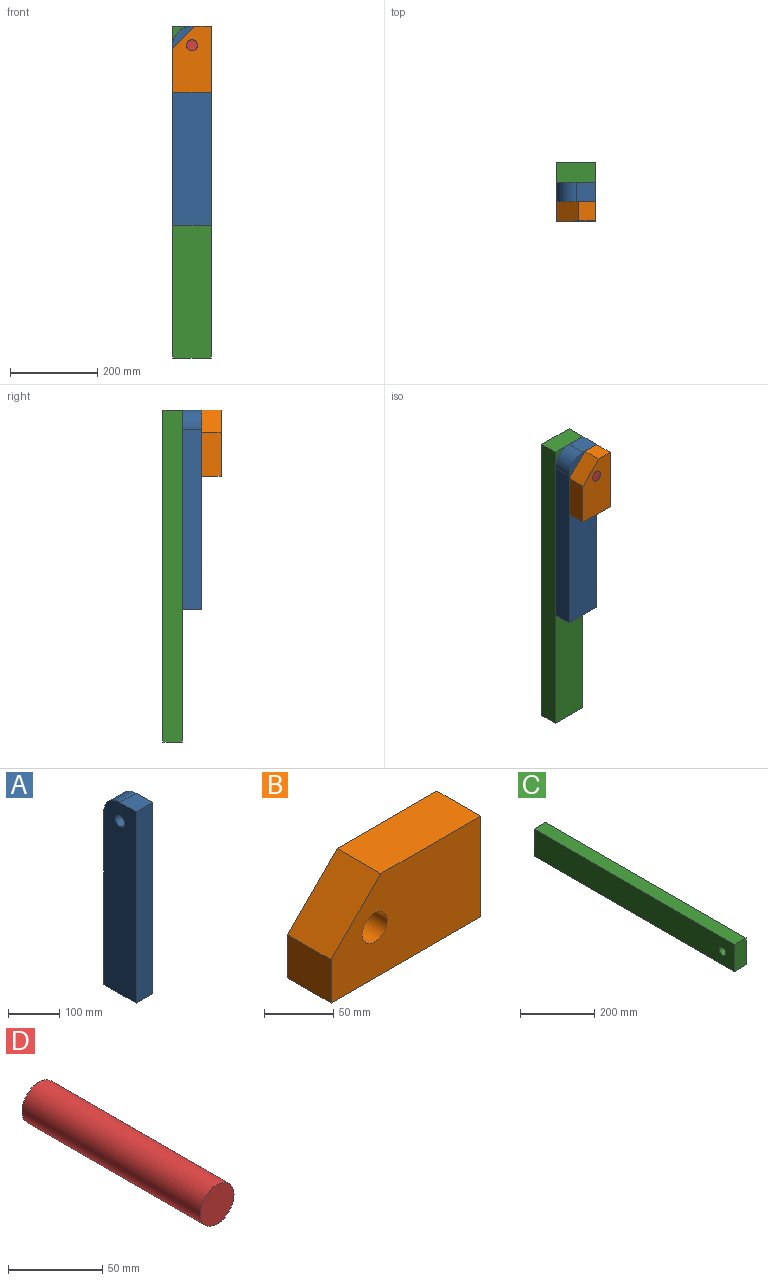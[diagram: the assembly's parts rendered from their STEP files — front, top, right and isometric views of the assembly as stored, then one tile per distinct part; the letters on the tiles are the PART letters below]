
ASSEMBLY  parts=4 mates=3
PART A: 8 faces, bbox 44.5x88.9x457.2 mm
  f0: plane 44.45x44.45mm, normal (0,0,1), area 1975.8mm2, adj f1,f5,f6,f7
  f1: plane 457.2x44.45mm, normal (0,-1,0), area 20322.5mm2, adj f0,f2,f6,f7
  f2: plane 88.9x44.45mm, normal (0,0,-1), area 3951.6mm2, adj f1,f3,f6,f7
  f3: plane 412.75x44.45mm, normal (0,1,0), area 18346.7mm2, adj f2,f5,f6,f7
  f4: cylinder r=12.7mm len=44.45mm, axis (-1,0,0), area 3547mm2, adj f6,f7
  f5: cylinder r=44.45mm len=44.45mm, axis (-1,0,0), area 3103.6mm2, adj f0,f3,f6,f7
  f6: plane 457.2x88.9mm, normal (1,0,0), area 39714.4mm2, adj f0,f1,f2,f3,f4,f5
  f7: plane 457.2x88.9mm, normal (-1,0,0), area 39714.4mm2, adj f0,f1,f2,f3,f4,f5
PART B: 8 faces, bbox 152.4x44.5x88.9 mm
  f0: plane 101.6x44.45mm, normal (0,0,1), area 4516.1mm2, adj f1,f4,f6,f7
  f1: plane 50.8x50.8mm, normal (-0.71,0,0.71), area 3193.4mm2, adj f0,f2,f6,f7
  f2: plane 44.45x38.1mm, normal (-1,0,0), area 1693.5mm2, adj f1,f3,f6,f7
  f3: plane 152.4x44.45mm, normal (0,0,-1), area 6774.2mm2, adj f2,f4,f6,f7
  f4: plane 88.9x44.45mm, normal (1,0,0), area 3951.6mm2, adj f0,f3,f6,f7
  f5: cylinder r=12.7mm len=44.45mm, axis (0,1,0), area 3547mm2, adj f6,f7
  f6: plane 152.4x88.9mm, normal (0,-1,0), area 11751.3mm2, adj f0,f1,f2,f3,f4,f5
  f7: plane 152.4x88.9mm, normal (0,1,0), area 11751.3mm2, adj f0,f1,f2,f3,f4,f5
PART C: 7 faces, bbox 44.5x762x88.9 mm
  f0: plane 762x88.9mm, normal (-1,0,0), area 67235.1mm2, adj f1,f3,f4,f5,f6
  f1: plane 762x44.45mm, normal (0,0,-1), area 33870.9mm2, adj f0,f2,f4,f5
  f2: plane 762x88.9mm, normal (1,0,0), area 67235.1mm2, adj f1,f3,f4,f5,f6
  f3: plane 762x44.45mm, normal (0,0,1), area 33870.9mm2, adj f0,f2,f4,f5
  f4: plane 88.9x44.45mm, normal (0,-1,0), area 3951.6mm2, adj f0,f1,f2,f3
  f5: plane 88.9x44.45mm, normal (0,1,0), area 3951.6mm2, adj f0,f1,f2,f3
  f6: cylinder r=12.7mm len=44.45mm, axis (1,0,0), area 3547mm2, adj f0,f2
PART D: 3 faces, bbox 25.4x133.4x25.4 mm
  f0: cylinder r=12.7mm len=133.35mm, axis (0,1,0), area 10640.9mm2, adj f1,f2
  f1: plane 25.4x25.4mm, normal (0,-1,0), area 506.7mm2, adj f0
  f2: plane 25.4x25.4mm, normal (0,1,0), area 506.7mm2, adj f0
PLACE A rot(axis=(0,0,1),90deg) t=(266.41,-374.73,1470.92)mm
PLACE B rot(axis=(0.71,0,-0.71),180deg) t=(266.41,-419.18,1470.92)mm
PLACE C rot(axis=(-0.58,0.58,-0.58),120deg) t=(177.51,-285.83,708.92)mm
PLACE D rot(axis=(0,0,-1),180deg) t=(221.96,-419.18,1426.47)mm
MATE fastened D.f0 <-> C.f6  axis (0,1,0) through (221.96,-285.83,1426.47)mm
MATE revolute D.f0 <-> B.f5  axis (0,-1,0) through (221.96,-419.18,1426.47)mm
MATE revolute A.f4 <-> D.f0  axis (0,-1,0) through (221.96,-352.51,1426.47)mm
